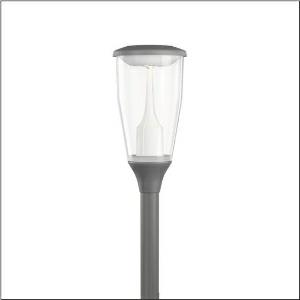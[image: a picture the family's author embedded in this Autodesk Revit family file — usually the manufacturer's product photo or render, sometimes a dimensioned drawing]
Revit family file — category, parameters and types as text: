
# Revit family: dl_11_iq___st1_2a_5xa5575mf14h000022_93a8
name_source: partatom
category: Lighting Fixtures
units: mm (PartAtom-declared; Revit-internal decimal feet)

## family parameters
Cut with Voids When Loaded = No
Host = Face
Light Source = No
Part Type = Normal
Room Calculation Point = No
Round Connector Dimension = Use Diameter
Shared = No

## types (1)
- --- (1 x LED, 1560 lm, 11.8 W, 2700K)
    Apparent Load = 12 VA
    CIE Flux Codes = 24 63 94 96 100
    Color Rendering = 70
    Color Temperature = 2700K
    Default Elevation = 1800 mm
    Description = DL 11 iQ, mast luminaire, Module 540 iQ-SR, primary light control with 3 zone facetted reflector, of plastic, silver coated, highly specular, structured, primary optical cover: cover, of PMMA, transparent, light distribution: ST1.2a, light emission: direct distribution, primary light characteristic: asymmetric, installation type: post-top, LED, High Power LED, rated luminous flux: 1.560lm, luminous efficacy: 149lm/W, light colour: 727, colour temperature: 2700K, control gear: iQ Street-Remote, control: Street-Remote, Auto-Match, Temp-Guard, Lumen-Switch, Night-Set, Smart-Wire, Light-Fading, Desk-Remote (wireless, voltage-free reading and setting of iQ features in the workshop via application-optimized NFC function/RFID function), optimised constant luminous flux control (CLO 2.0), mains connection: 220..240V, AC, 50/60Hz, connection cable pre-assembled, cable length: 5,5m, wiring characteristics: H07RN-F, 5-core, 1.5mm², start of lifetime: 12W, end of service life: 12W, reduction: 5W, luminaire housing, upper part, of diecast aluminium, coated, SITECO metallic grey (DB 702S), spigot size: 76mm (post-top), mounting height: 3..5m, post-top mast mounting element, of diecast aluminium, coated, SITECO metallic grey (DB 702S), Module 540 iQ-SR, traffic white (RAL 9016), equipment: standard, protection rating (complete): IP66, insulation class (complete): insulation class II (safety insulation), certification: CE, ENEC, ENEC+, VDE, impact resistance: IK07, packaging unit: 1 piece

Light Distribution: ST1.2a
    Height = 665 mm
    Lamp = 1 x LED
    Lamp Light Flux = 1560 lm
    Lamp Power = 11.8 W
    Lamp count = 1
    Length = 334 mm
    Luminous efficacy = 132 lm/W
    Manufacturer = Siteco
    ModVariant = No
    Model = 5XA5575MF14H000022
    Number of Poles = 1
    OnlyDefault = Yes
    Power Factor = 1
    Product Name = DL 11 iQ | ST1.2a
    Product group = mast luminaire | pylon top
    ProductGroupID = 6100
    Protection Class = Protection class II
    Protection Degree = IP 66
    RLX_Detail_Level = 1
    RLX_Emergency_Light_Flux = 0 lm
    RLX_Emergency_Type = 0
    RLX_Emergency_Type_DB = No
    RlxData = <blob elided: 153613 chars, md5=142ce7e3>
    Socket = socket
    Standby Power = 0 W
    System Light Flux = 1560 lm
    System Power = 12 W
    Type Comments = factory setting: luminous flux: 100 % | dim-lin: 254 | 472 mA
    Type Image = l_1258354.jpg
    URL = http://relux.com
    VarID = @adj_098759
    Voltage = 0 V
    Weight = 0.00 kg
    Width = 0 mm  [stored 0 ft]

note: [stored X ft] marks values corroborated as IEEE doubles in the binary element streams (Revit-internal decimal feet)

## geometry (parser evidence)
native form markers: Blend x4, Sweep x12
no freeform markers — native parametric forms only
